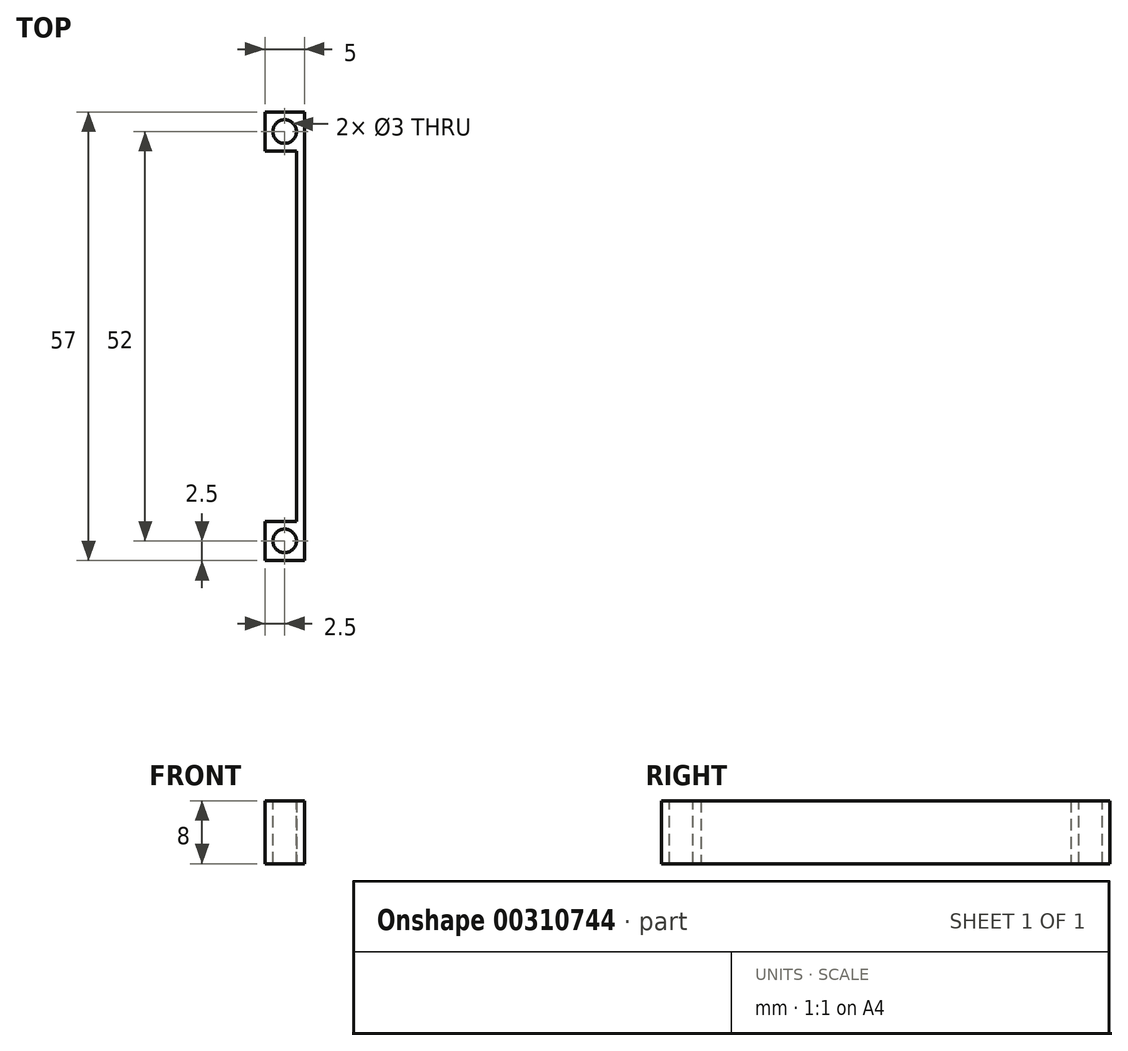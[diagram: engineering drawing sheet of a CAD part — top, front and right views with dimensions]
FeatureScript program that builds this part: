
annotation { "Feature Type Name" : "Feature", "Feature Type Description" : "" }
export const myFeature = defineFeature(function(context is Context, id is Id, definition is map)
    precondition{}
    {
        {
            var Q0;
            Q0=qCreatedBy(makeId("Top.planeOp"),FACE);
            var sketch = newSketch(context, id + "F0", { "sketchPlane" : qUnion([Q0])});
            skLineSegment(sketch, "E0", {"start": v(0, 0) * mm, "end": v(5, 0) * mm});
            skLineSegment(sketch, "E1", {"start": v(5, 0) * mm, "end": v(5, 5) * mm});
            skLineSegment(sketch, "E2", {"start": v(5, 5) * mm, "end": v(0, 5) * mm});
            skLineSegment(sketch, "E3", {"start": v(0, 5) * mm, "end": v(0, 0) * mm});
            skSolve(sketch);
        }
        {
            var Q0;
            Q0=makeQuery(id+"F0.imprint","IMPRINT",FACE,{"disambiguationData":[TD([[makeQuery(id+"F0.imprint","IMPRINT",EDGE,{"derivedFrom":sQuery(id+"F0.wireOp",EDGE,"E0")}),1.0]])]});
            extrude(context, id + "F1", {"entities" : qUnion([Q0]), "depth" : 8 * mm});
        }
        {
            var Q0;
            Q0=makeQuery(id+"F1.opExtrude","CAP_FACE",FACE,{"disambiguationData":[OSD([sQuery(id+"F0.wireOp",EDGE,"E0"),sQuery(id+"F0.wireOp",EDGE,"E1"),sQuery(id+"F0.wireOp",EDGE,"E2"),sQuery(id+"F0.wireOp",EDGE,"E3")])],"isStart":false});
            var sketch = newSketch(context, id + "F2", { "sketchPlane" : qUnion([Q0])});
            skCircle(sketch, "E4", {"center": v(2.5, 2.5) * mm, "radius": 1.5 * mm});
            skPoint(sketch, "E4.centerSnap0", {"position": v(2.5, 5) * mm});
            skPoint(sketch, "E4.centerSnap1", {"position": v(5, 2.5) * mm});
            skSolve(sketch);
        }
        {
            var Q0;
            Q0=makeQuery(id+"F2.imprint","IMPRINT",FACE,{"disambiguationData":[TD([[makeQuery(id+"F2.imprint","IMPRINT",EDGE,{"derivedFrom":sQuery(id+"F2.wireOp",EDGE,"E4")}),1.0]])]});
            extrude(context, id + "F3", {"entities" : qUnion([Q0]), "operationType" : NewBodyOperationType.REMOVE, "oppositeDirection" : true, "depth" : 25 * mm});
        }
        {
            var Q0;
            Q0=makeQuery(id+"F1.opExtrude","SWEPT_FACE",FACE,{"disambiguationData":[OSD([sQuery(id+"F0.wireOp",EDGE,"E0")])]});
            var sketch = newSketch(context, id + "F4", { "sketchPlane" : qUnion([Q0])});
            skLineSegment(sketch, "E5", {"start": v(5, 8) * mm, "end": v(4, 8) * mm});
            skLineSegment(sketch, "E6", {"start": v(4, 8) * mm, "end": v(4, 0) * mm});
            skLineSegment(sketch, "E7", {"start": v(4, 0) * mm, "end": v(5, 0) * mm});
            skLineSegment(sketch, "E8", {"start": v(5, 0) * mm, "end": v(5, 8) * mm});
            skSolve(sketch);
        }
        {
            var Q0;
            Q0=makeQuery(id+"F4.imprint","IMPRINT",FACE,{"disambiguationData":[TD([[makeQuery(id+"F4.imprint","IMPRINT",EDGE,{"derivedFrom":sQuery(id+"F4.wireOp",EDGE,"E5")}),-1.0]])]});
            extrude(context, id + "F5", {"entities" : qUnion([Q0]), "operationType" : NewBodyOperationType.ADD, "depth" : 47 * mm});
        }
        {
            var Q0;
            Q0=makeQuery(id+"F5.opExtrude","CAP_FACE",FACE,{"disambiguationData":[OSD([sQuery(id+"F4.wireOp",EDGE,"E5"),sQuery(id+"F4.wireOp",EDGE,"E6"),sQuery(id+"F4.wireOp",EDGE,"E7"),sQuery(id+"F4.wireOp",EDGE,"E8")])],"isStart":false});
            var sketch = newSketch(context, id + "F6", { "sketchPlane" : qUnion([Q0])});
            skLineSegment(sketch, "E9", {"start": v(5, 8) * mm, "end": v(0, 8) * mm});
            skLineSegment(sketch, "E10", {"start": v(0, 8) * mm, "end": v(0, 0) * mm});
            skLineSegment(sketch, "E11", {"start": v(0, 0) * mm, "end": v(5, 0) * mm});
            skSolve(sketch);
        }
        {
            var Q0;
            {var subQ2=makeQuery(id+"F5.opExtrude","CAP_EDGE",EDGE,{"disambiguationData":[OSD([sQuery(id+"F4.wireOp",EDGE,"E6")])],"isStart":false});Q0=makeQuery(id+"F6.imprint","IMPRINT",FACE,{"disambiguationData":[TD([[makeQuery(id+"F6.imprint","IMPRINT",EDGE,{"derivedFrom":subQ2}),1.0]])]});}
            var Q1;
            {var subQ2=sQuery(id+"F6.wireOp",EDGE,"E10");Q1=makeQuery(id+"F6.imprint","IMPRINT",FACE,{"disambiguationData":[TD([[makeQuery(id+"F6.imprint","IMPRINT",EDGE,{"derivedFrom":subQ2}),1.0]])]});}
            extrude(context, id + "F7", {"entities" : qUnion([Q0, Q1]), "operationType" : NewBodyOperationType.ADD, "depth" : 5 * mm});
        }
        {
            var Q0;
            Q0=makeQuery(id+"F7.boolean.opBoolean","MERGE",FACE,{"derivedFrom":[makeQuery(id+"F5.boolean.opBoolean","MERGE",FACE,{"derivedFrom":[makeQuery(id+"F1.opExtrude","CAP_FACE",FACE,{"disambiguationData":[OSD([sQuery(id+"F0.wireOp",EDGE,"E0"),sQuery(id+"F0.wireOp",EDGE,"E1"),sQuery(id+"F0.wireOp",EDGE,"E2"),sQuery(id+"F0.wireOp",EDGE,"E3")])],"isStart":false}),makeQuery(id+"F5.opExtrude","SWEPT_FACE",FACE,{"disambiguationData":[OSD([sQuery(id+"F4.wireOp",EDGE,"E5")])]})]}),makeQuery(id+"F7.opExtrude","SWEPT_FACE",FACE,{"disambiguationData":[OSD([sQuery(id+"F6.wireOp",EDGE,"E9")])]})]});
            var sketch = newSketch(context, id + "F8", { "sketchPlane" : qUnion([Q0])});
            skCircle(sketch, "E12", {"center": v(2.5, -49.5) * mm, "radius": 1.5 * mm});
            skPoint(sketch, "E12.centerSnap0", {"position": v(0, -49.5) * mm});
            skPoint(sketch, "E12.centerSnap1", {"position": v(2.5, -52) * mm});
            skSolve(sketch);
        }
        {
            var Q0;
            Q0=makeQuery(id+"F8.imprint","IMPRINT",FACE,{"disambiguationData":[TD([[makeQuery(id+"F8.imprint","IMPRINT",EDGE,{"derivedFrom":sQuery(id+"F8.wireOp",EDGE,"E12")}),1.0]])]});
            extrude(context, id + "F9", {"entities" : qUnion([Q0]), "operationType" : NewBodyOperationType.REMOVE, "oppositeDirection" : true, "depth" : 25 * mm});
        }
    });
